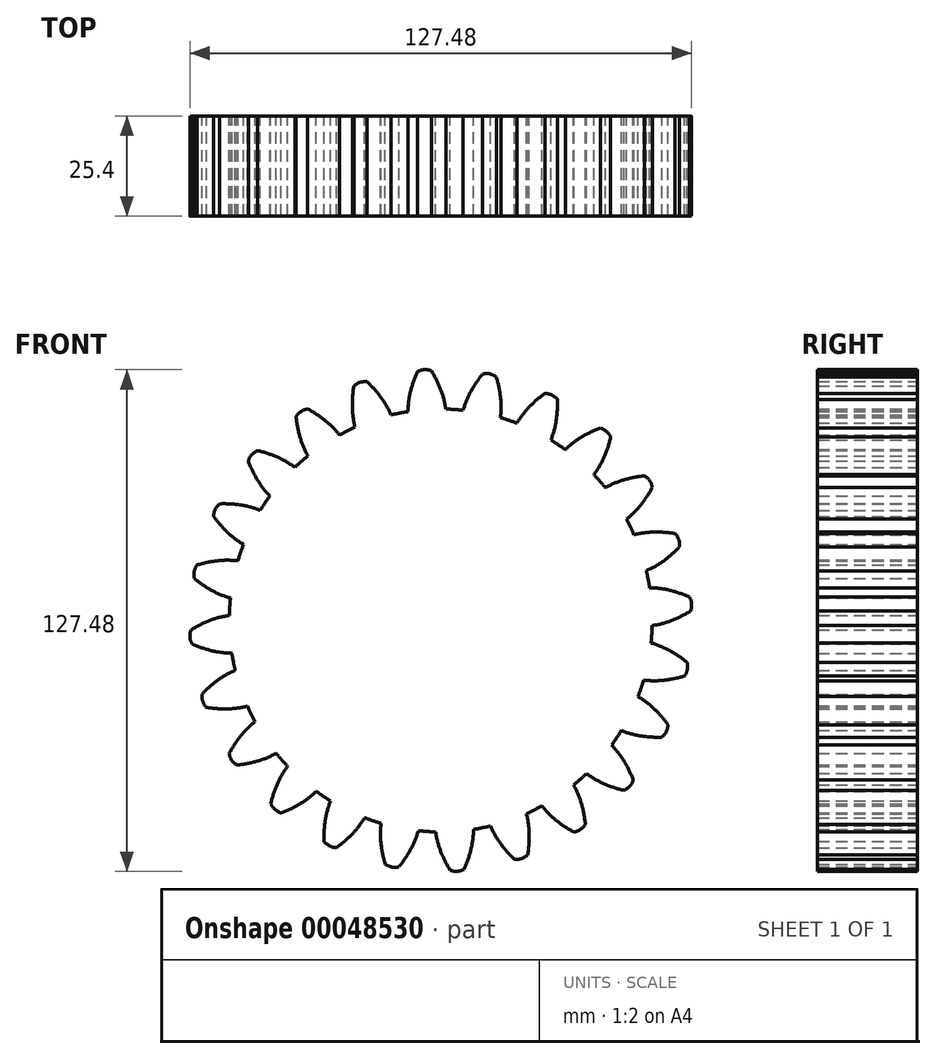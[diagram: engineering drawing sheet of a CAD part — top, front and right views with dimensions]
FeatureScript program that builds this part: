
annotation { "Feature Type Name" : "Feature", "Feature Type Description" : "" }
export const myFeature = defineFeature(function(context is Context, id is Id, definition is map)
    precondition{}
    {
        {
            var Q0;
            Q0=qCreatedBy(makeId("Front.planeOp"),FACE);
            var sketch = newSketch(context, id + "F0", { "sketchPlane" : qUnion([Q0])});
            skCircle(sketch, "E0", {"center": v(0, 0) * mm, "radius": 53.72 * mm});
            skCircle(sketch, "E1", {"center": v(0, 0) * mm, "radius": 58.67 * mm, "construction": true});
            skCircle(sketch, "E2", {"center": v(0, 0) * mm, "radius": 63.5 * mm, "construction": true});
            skLineSegment(sketch, "E3", {"start": v(0, 0) * mm, "end": v(0, 106.16) * mm, "construction": true});
            skLineSegment(sketch, "E4", {"start": v(0, 0) * mm, "end": v(-6.87, 104.56) * mm, "construction": true});
            skLineSegment(sketch, "E5", {"start": v(0, 58.67) * mm, "end": v(-99.18, 58.67) * mm, "construction": true});
            skLineSegment(sketch, "E6", {"start": v(0, 58.67) * mm, "end": v(-95.27, 24) * mm, "construction": true});
            skCircle(sketch, "E7", {"center": v(0, 58.67) * mm, "radius": 25.07 * mm, "construction": true});
            skCircle(sketch, "E8", {"center": v(0, 0) * mm, "radius": 55.14 * mm, "construction": true});
            skCircle(sketch, "E9", {"center": v(-23.48, 49.89) * mm, "radius": 25.07 * mm, "construction": true});
            skArc(sketch, "E10", {"start": v(0, 58.67) * mm, "mid": v(-1.09, 61.12) * mm, "end": v(-2.4, 63.45) * mm});
            skArc(sketch, "E11", {"start": v(1.3, 53.7) * mm, "mid": v(0.8, 56.23) * mm, "end": v(0, 58.67) * mm});
            skArc(sketch, "E12.MirrorCS", {"start": v(-8.31, 53.07) * mm, "mid": v(-8.14, 55.64) * mm, "end": v(-7.67, 58.17) * mm});
            skArc(sketch, "E13.MirrorCS", {"start": v(-7.67, 58.17) * mm, "mid": v(-6.91, 60.74) * mm, "end": v(-5.92, 63.22) * mm});
            skArc(sketch, "E14", {"start": v(-2.4, 63.45) * mm, "mid": v(-4.19, 63.73) * mm, "end": v(-5.92, 63.22) * mm});
            skSolve(sketch);
        }
        {
            var Q0;
            {var subQ0=sQuery(id+"F0.wireOp",EDGE,"E0");var subQ2=makeQuery(id+"F0.imprint","INTERSECT",VERTEX,{"derivedFrom":[subQ0,sQuery(id+"F0.wireOp",EDGE,"E11")]});Q0=makeQuery(id+"F0.imprint","IMPRINT",FACE,{"disambiguationData":[TD([[makeQuery(id+"F0.imprint","IMPRINT",EDGE,{"disambiguationData":[TD([[subQ2,-1.0]])],"derivedFrom":subQ0}),1.0]])]});}
            var Q1;
            Q1=makeQuery(id+"F0.imprint","IMPRINT",FACE,{"disambiguationData":[TD([[makeQuery(id+"F0.imprint","IMPRINT",EDGE,{"derivedFrom":sQuery(id+"F0.wireOp",EDGE,"E10")}),1.0]])]});
            extrude(context, id + "F1", {"entities" : qUnion([Q0, Q1]), "depth" : 25.4 * mm});
        }
        {
            var Q0;
            Q0=makeQuery(id+"F1.opExtrude","SWEPT_BODY",BODY,{"disambiguationData":[OSD([sQuery(id+"F0.wireOp",EDGE,"E0"),sQuery(id+"F0.wireOp",EDGE,"E10"),sQuery(id+"F0.wireOp",EDGE,"E11"),sQuery(id+"F0.wireOp",EDGE,"E12.MirrorCS"),sQuery(id+"F0.wireOp",EDGE,"E13.MirrorCS"),sQuery(id+"F0.wireOp",EDGE,"E14")])]});
            var Q1;
            Q1=makeQuery(id+"F1.opExtrude","SWEPT_FACE",FACE,{"disambiguationData":[OSD([sQuery(id+"F0.wireOp",EDGE,"E14")])]});
            var Q2;
            Q2=makeQuery(id+"F1.opExtrude","SWEPT_FACE",FACE,{"disambiguationData":[OSD([sQuery(id+"F0.wireOp",EDGE,"E11")])]});
            var Q3;
            Q3=makeQuery(id+"F1.opExtrude","SWEPT_FACE",FACE,{"disambiguationData":[OSD([sQuery(id+"F0.wireOp",EDGE,"E10")])]});
            var Q4;
            Q4=makeQuery(id+"F1.opExtrude","SWEPT_FACE",FACE,{"disambiguationData":[OSD([sQuery(id+"F0.wireOp",EDGE,"E13.MirrorCS")])]});
            var Q5;
            Q5=makeQuery(id+"F1.opExtrude","SWEPT_FACE",FACE,{"disambiguationData":[OSD([sQuery(id+"F0.wireOp",EDGE,"E12.MirrorCS")])]});
            var Q6;
            Q6=makeQuery(id+"F1.opExtrude","CAP_EDGE",EDGE,{"disambiguationData":[OSD([sQuery(id+"F0.wireOp",EDGE,"E0")])],"isStart":false});
            circularPattern(context, id + "F2", {"faces" : qUnion([Q1, Q2, Q3, Q4, Q5]), "axis" : qUnion([Q6]), "angle" : 15 * degree, "instanceCount" : 24, "oppositeDirection" : true, "patternType" : PatternType.FACE});
        }
    });
